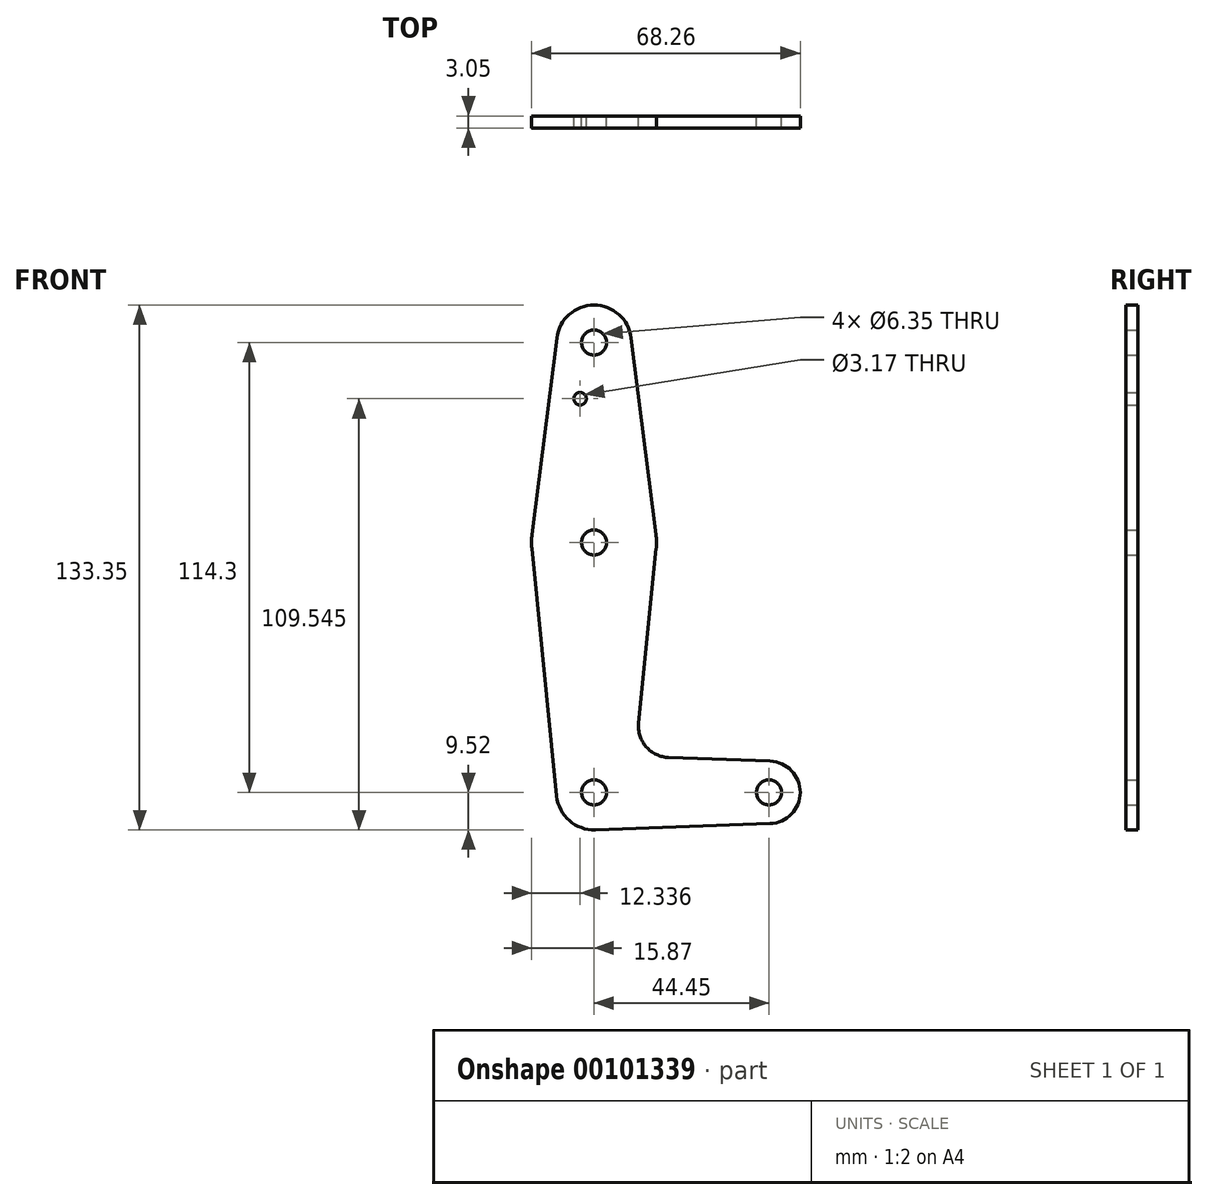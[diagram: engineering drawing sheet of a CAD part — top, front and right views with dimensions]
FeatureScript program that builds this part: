
annotation { "Feature Type Name" : "Feature", "Feature Type Description" : "" }
export const myFeature = defineFeature(function(context is Context, id is Id, definition is map)
    precondition{}
    {
        {
            var Q0;
            Q0=qCreatedBy(makeId("Front.planeOp"),FACE);
            var sketch = newSketch(context, id + "F0", { "sketchPlane" : qUnion([Q0])});
            skLineSegment(sketch, "E0", {"start": v(0, 114.3) * mm, "end": v(0, 0) * mm});
            skLineSegment(sketch, "E1", {"start": v(0, 0) * mm, "end": v(44.45, 0) * mm});
            skCircle(sketch, "E2", {"center": v(0, 114.3) * mm, "radius": 9.53 * mm});
            skCircle(sketch, "E3", {"center": v(0, 63.5) * mm, "radius": 15.88 * mm});
            skCircle(sketch, "E4", {"center": v(0, 0) * mm, "radius": 9.53 * mm});
            skCircle(sketch, "E5", {"center": v(44.45, 0) * mm, "radius": 7.94 * mm});
            skPoint(sketch, "E6.startSnap0", {"position": v(0, 57.15) * mm});
            skLineSegment(sketch, "E7", {"start": v(9.45, 115.5) * mm, "end": v(15.75, 65.48) * mm});
            skLineSegment(sketch, "E8", {"start": v(-9.45, 115.5) * mm, "end": v(-15.75, 65.48) * mm});
            skLineSegment(sketch, "E9", {"start": v(-9.48, -0.95) * mm, "end": v(-15.8, 61.91) * mm});
            skLineSegment(sketch, "E10", {"start": v(15.8, 61.91) * mm, "end": v(11.34, 17.6) * mm});
            skLineSegment(sketch, "E11", {"start": v(18.97, 8.85) * mm, "end": v(44.73, 7.93) * mm});
            skLineSegment(sketch, "E12", {"start": v(0.34, -9.52) * mm, "end": v(44.73, -7.93) * mm});
            skCircle(sketch, "E13", {"center": v(0, 114.3) * mm, "radius": 3.18 * mm});
            skCircle(sketch, "E14", {"center": v(0, 63.5) * mm, "radius": 3.18 * mm});
            skCircle(sketch, "E15", {"center": v(0, 0) * mm, "radius": 3.18 * mm});
            skCircle(sketch, "E16", {"center": v(44.45, 0) * mm, "radius": 3.18 * mm});
            skCircle(sketch, "E17", {"center": v(-3.53, 100.03) * mm, "radius": 1.59 * mm});
            skArc(sketch, "E18.filletArc", {"start": v(11.34, 17.6) * mm, "mid": v(13.26, 11.57) * mm, "end": v(18.97, 8.85) * mm});
            skSolve(sketch);
        }
        {
            var Q0;
            Q0 = qSketchRegion(id + "F0", true);
            var Q1;
            {var subQ0=sQuery(id+"F0.wireOp",EDGE,"E4");var subQ1=sQuery(id+"F0.wireOp",EDGE,"E0");var subQ2=makeQuery(id+"F0.imprint","INTERSECT",VERTEX,{"derivedFrom":[subQ1,subQ0]});Q1=makeQuery(id+"F0.imprint","IMPRINT",FACE,{"disambiguationData":[TD([[makeQuery(id+"F0.imprint","IMPRINT",EDGE,{"disambiguationData":[TD([[subQ2,-1.0]])],"derivedFrom":subQ1}),1.0]])]});}
            extrude(context, id + "F1", {"entities" : qUnion([Q0, Q1]), "depth" : 3.05 * mm});
        }
    });
